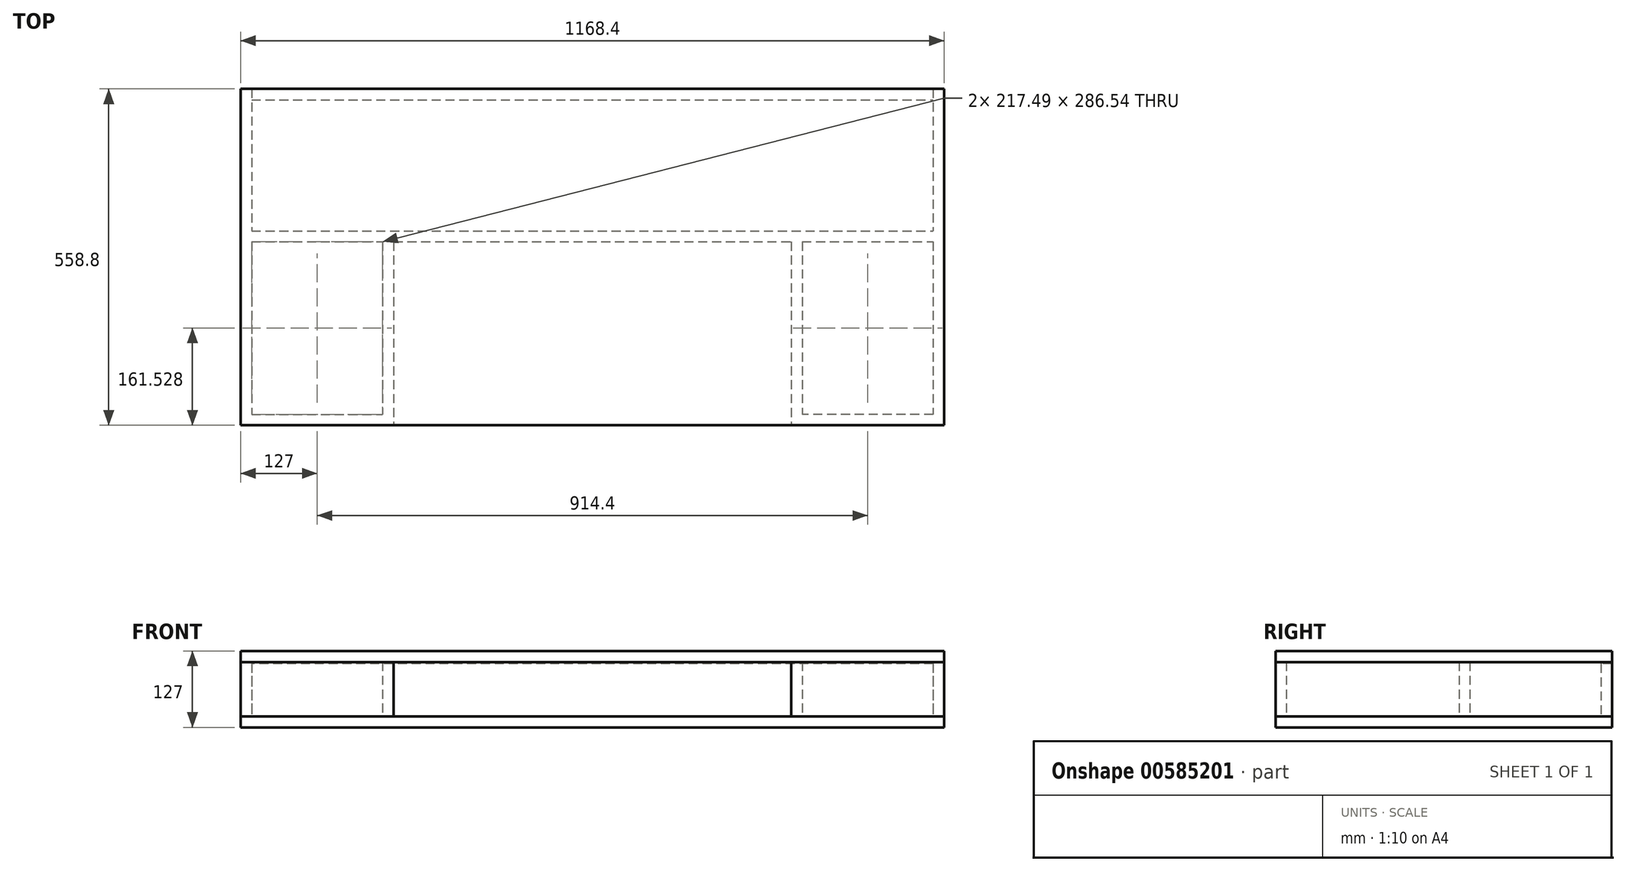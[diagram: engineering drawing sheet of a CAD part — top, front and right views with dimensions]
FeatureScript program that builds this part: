
annotation { "Feature Type Name" : "Feature", "Feature Type Description" : "" }
export const myFeature = defineFeature(function(context is Context, id is Id, definition is map)
    precondition{}
    {
        {
            var Q0;
            Q0=qCreatedBy(makeId("Top.planeOp"),FACE);
            var sketch = newSketch(context, id + "F0", { "sketchPlane" : qUnion([Q0])});
            skLineSegment(sketch, "E0.rect.bottom", {"start": v(584.2, 279.4) * mm, "end": v(-584.2, 279.4) * mm});
            skLineSegment(sketch, "E0.rect.top", {"start": v(584.2, -279.4) * mm, "end": v(-584.2, -279.4) * mm});
            skLineSegment(sketch, "E0.rect.left", {"start": v(584.2, 279.4) * mm, "end": v(584.2, -279.4) * mm});
            skLineSegment(sketch, "E0.rect.right", {"start": v(-584.2, 279.4) * mm, "end": v(-584.2, -279.4) * mm});
            skPoint(sketch, "E0.rect.middle", {"position": v(0, 0) * mm});
            skSolve(sketch);
        }
        {
            var Q0;
            Q0=qSketchRegion(id+"F0",true);
            extrude(context, id + "F1", {"entities" : qUnion([Q0]), "depth" : 18.26 * mm, "offsetDistance" : 25.4 * mm});
        }
        {
            var Q0;
            Q0=makeQuery(id+"F1.opExtrude","CAP_FACE",FACE,{"disambiguationData":[OSD([sQuery(id+"F0.wireOp",EDGE,"E0.rect.bottom"),sQuery(id+"F0.wireOp",EDGE,"E0.rect.top"),sQuery(id+"F0.wireOp",EDGE,"E0.rect.left"),sQuery(id+"F0.wireOp",EDGE,"E0.rect.right")])],"isStart":false});
            var sketch = newSketch(context, id + "F2", { "sketchPlane" : qUnion([Q0])});
            skLineSegment(sketch, "E1.bottom", {"start": v(-565.94, 43.66) * mm, "end": v(565.94, 43.66) * mm});
            skLineSegment(sketch, "E1.top", {"start": v(-565.94, 25.4) * mm, "end": v(565.94, 25.4) * mm});
            skLineSegment(sketch, "E1.left", {"start": v(-565.94, 43.66) * mm, "end": v(-565.94, 25.4) * mm});
            skLineSegment(sketch, "E1.right", {"start": v(565.94, 43.66) * mm, "end": v(565.94, 25.4) * mm});
            skLineSegment(sketch, "E2.rect.bottom", {"start": v(-330.2, -279.4) * mm, "end": v(330.2, -279.4) * mm, "construction": true});
            skLineSegment(sketch, "E2.rect.top", {"start": v(-330.2, 279.4) * mm, "end": v(330.2, 279.4) * mm, "construction": true});
            skLineSegment(sketch, "E2.rect.left", {"start": v(-330.2, -279.4) * mm, "end": v(-330.2, 279.4) * mm, "construction": true});
            skLineSegment(sketch, "E2.rect.right", {"start": v(330.2, -279.4) * mm, "end": v(330.2, 279.4) * mm, "construction": true});
            skPoint(sketch, "E2.rect.middle", {"position": v(0, 0) * mm});
            skPoint(sketch, "E2.rect.middle.positionSnap0", {"position": v(0, 43.66) * mm});
            skPoint(sketch, "E2.rect.centerSnap0", {"position": v(0, 43.66) * mm});
            skLineSegment(sketch, "E3.bottom", {"start": v(-330.2, 25.4) * mm, "end": v(-348.46, 25.4) * mm});
            skLineSegment(sketch, "E3.top", {"start": v(-330.2, -261.14) * mm, "end": v(-348.46, -261.14) * mm});
            skLineSegment(sketch, "E3.left", {"start": v(-330.2, 25.4) * mm, "end": v(-330.2, -261.14) * mm});
            skLineSegment(sketch, "E3.right", {"start": v(-348.46, 25.4) * mm, "end": v(-348.46, -261.14) * mm});
            skLineSegment(sketch, "E4.bottom", {"start": v(330.2, 25.4) * mm, "end": v(348.46, 25.4) * mm});
            skLineSegment(sketch, "E4.top", {"start": v(330.2, -261.14) * mm, "end": v(348.46, -261.14) * mm});
            skLineSegment(sketch, "E4.left", {"start": v(330.2, 25.4) * mm, "end": v(330.2, -261.14) * mm});
            skLineSegment(sketch, "E4.right", {"start": v(348.46, 25.4) * mm, "end": v(348.46, -261.14) * mm});
            skLineSegment(sketch, "E5.bottom", {"start": v(-584.2, 279.4) * mm, "end": v(-565.94, 279.4) * mm});
            skLineSegment(sketch, "E5.top", {"start": v(-584.2, -261.14) * mm, "end": v(-565.94, -261.14) * mm});
            skLineSegment(sketch, "E5.left", {"start": v(-584.2, 279.4) * mm, "end": v(-584.2, -261.14) * mm});
            skLineSegment(sketch, "E5.right", {"start": v(-565.94, 279.4) * mm, "end": v(-565.94, -261.14) * mm});
            skLineSegment(sketch, "E6.bottom", {"start": v(584.2, 279.4) * mm, "end": v(565.94, 279.4) * mm});
            skLineSegment(sketch, "E6.top", {"start": v(584.2, -261.14) * mm, "end": v(565.94, -261.14) * mm});
            skLineSegment(sketch, "E6.left", {"start": v(584.2, 279.4) * mm, "end": v(584.2, -261.14) * mm});
            skLineSegment(sketch, "E6.right", {"start": v(565.94, 279.4) * mm, "end": v(565.94, -261.14) * mm});
            skLineSegment(sketch, "E7.bottom", {"start": v(-584.2, -261.14) * mm, "end": v(-330.2, -261.14) * mm});
            skLineSegment(sketch, "E7.top", {"start": v(-584.2, -279.4) * mm, "end": v(-330.2, -279.4) * mm});
            skLineSegment(sketch, "E7.left", {"start": v(-584.2, -261.14) * mm, "end": v(-584.2, -279.4) * mm});
            skLineSegment(sketch, "E7.right", {"start": v(-330.2, -261.14) * mm, "end": v(-330.2, -279.4) * mm});
            skLineSegment(sketch, "E8.bottom", {"start": v(584.2, -261.14) * mm, "end": v(330.2, -261.14) * mm});
            skLineSegment(sketch, "E8.top", {"start": v(584.2, -279.4) * mm, "end": v(330.2, -279.4) * mm});
            skLineSegment(sketch, "E8.left", {"start": v(584.2, -261.14) * mm, "end": v(584.2, -279.4) * mm});
            skLineSegment(sketch, "E8.right", {"start": v(330.2, -261.14) * mm, "end": v(330.2, -279.4) * mm});
            skSolve(sketch);
        }
        {
            var Q0;
            Q0=qSketchRegion(id+"F2",true);
            extrude(context, id + "F3", {"entities" : qUnion([Q0]), "depth" : 90.49 * mm});
        }
        {
            var Q0;
            Q0=makeQuery(id+"F1.opExtrude","CAP_FACE",FACE,{"disambiguationData":[OSD([sQuery(id+"F0.wireOp",EDGE,"E0.rect.bottom"),sQuery(id+"F0.wireOp",EDGE,"E0.rect.top"),sQuery(id+"F0.wireOp",EDGE,"E0.rect.left"),sQuery(id+"F0.wireOp",EDGE,"E0.rect.right")])],"isStart":false});
            var sketch = newSketch(context, id + "F4", { "sketchPlane" : qUnion([Q0])});
            skLineSegment(sketch, "E9.bottom", {"start": v(-565.94, 279.4) * mm, "end": v(565.94, 279.4) * mm});
            skLineSegment(sketch, "E9.top", {"start": v(-565.94, 261.14) * mm, "end": v(565.94, 261.14) * mm});
            skLineSegment(sketch, "E9.left", {"start": v(-565.94, 279.4) * mm, "end": v(-565.94, 261.14) * mm});
            skLineSegment(sketch, "E9.right", {"start": v(565.94, 279.4) * mm, "end": v(565.94, 261.14) * mm});
            skSolve(sketch);
        }
        {
            var Q0;
            Q0=qSketchRegion(id+"F4",true);
            extrude(context, id + "F5", {"entities" : qUnion([Q0]), "depth" : 87.63 * mm});
        }
        {
            var Q0;
            Q0=makeQuery(id+"F3.opExtrude","CAP_FACE",FACE,{"disambiguationData":[OSD([sQuery(id+"F2.wireOp",EDGE,"E1.bottom"),sQuery(id+"F2.wireOp",EDGE,"E1.top"),sQuery(id+"F2.wireOp",EDGE,"E3.left"),sQuery(id+"F2.wireOp",EDGE,"E3.right"),sQuery(id+"F2.wireOp",EDGE,"E4.left"),sQuery(id+"F2.wireOp",EDGE,"E4.right"),sQuery(id+"F2.wireOp",EDGE,"E5.bottom"),sQuery(id+"F2.wireOp",EDGE,"E5.left"),sQuery(id+"F2.wireOp",EDGE,"E5.right"),sQuery(id+"F2.wireOp",EDGE,"E6.bottom"),sQuery(id+"F2.wireOp",EDGE,"E6.left"),sQuery(id+"F2.wireOp",EDGE,"E6.right"),sQuery(id+"F2.wireOp",EDGE,"E7.bottom"),sQuery(id+"F2.wireOp",EDGE,"E7.top"),sQuery(id+"F2.wireOp",EDGE,"E7.left"),sQuery(id+"F2.wireOp",EDGE,"E7.right"),sQuery(id+"F2.wireOp",EDGE,"E8.bottom"),sQuery(id+"F2.wireOp",EDGE,"E8.top"),sQuery(id+"F2.wireOp",EDGE,"E8.left"),sQuery(id+"F2.wireOp",EDGE,"E8.right"),sQuery(id+"F2.wireOp",EDGE,"5b780894-bd24-4c12-90cd-344abb398ec0.bottom"),sQuery(id+"F2.wireOp",EDGE,"5b780894-bd24-4c12-90cd-344abb398ec0.top")])],"isStart":false});
            var sketch = newSketch(context, id + "F6", { "sketchPlane" : qUnion([Q0])});
            skLineSegment(sketch, "E10.bottom", {"start": v(-584.2, 279.4) * mm, "end": v(584.2, 279.4) * mm});
            skLineSegment(sketch, "E10.top", {"start": v(-584.2, -279.4) * mm, "end": v(584.2, -279.4) * mm});
            skLineSegment(sketch, "E10.left", {"start": v(-584.2, 279.4) * mm, "end": v(-584.2, -279.4) * mm});
            skLineSegment(sketch, "E10.right", {"start": v(584.2, 279.4) * mm, "end": v(584.2, -279.4) * mm});
            skSolve(sketch);
        }
        {
            var Q0;
            Q0=qSketchRegion(id+"F6",true);
            extrude(context, id + "F7", {"entities" : qUnion([Q0]), "depth" : 18.26 * mm});
        }
    });
